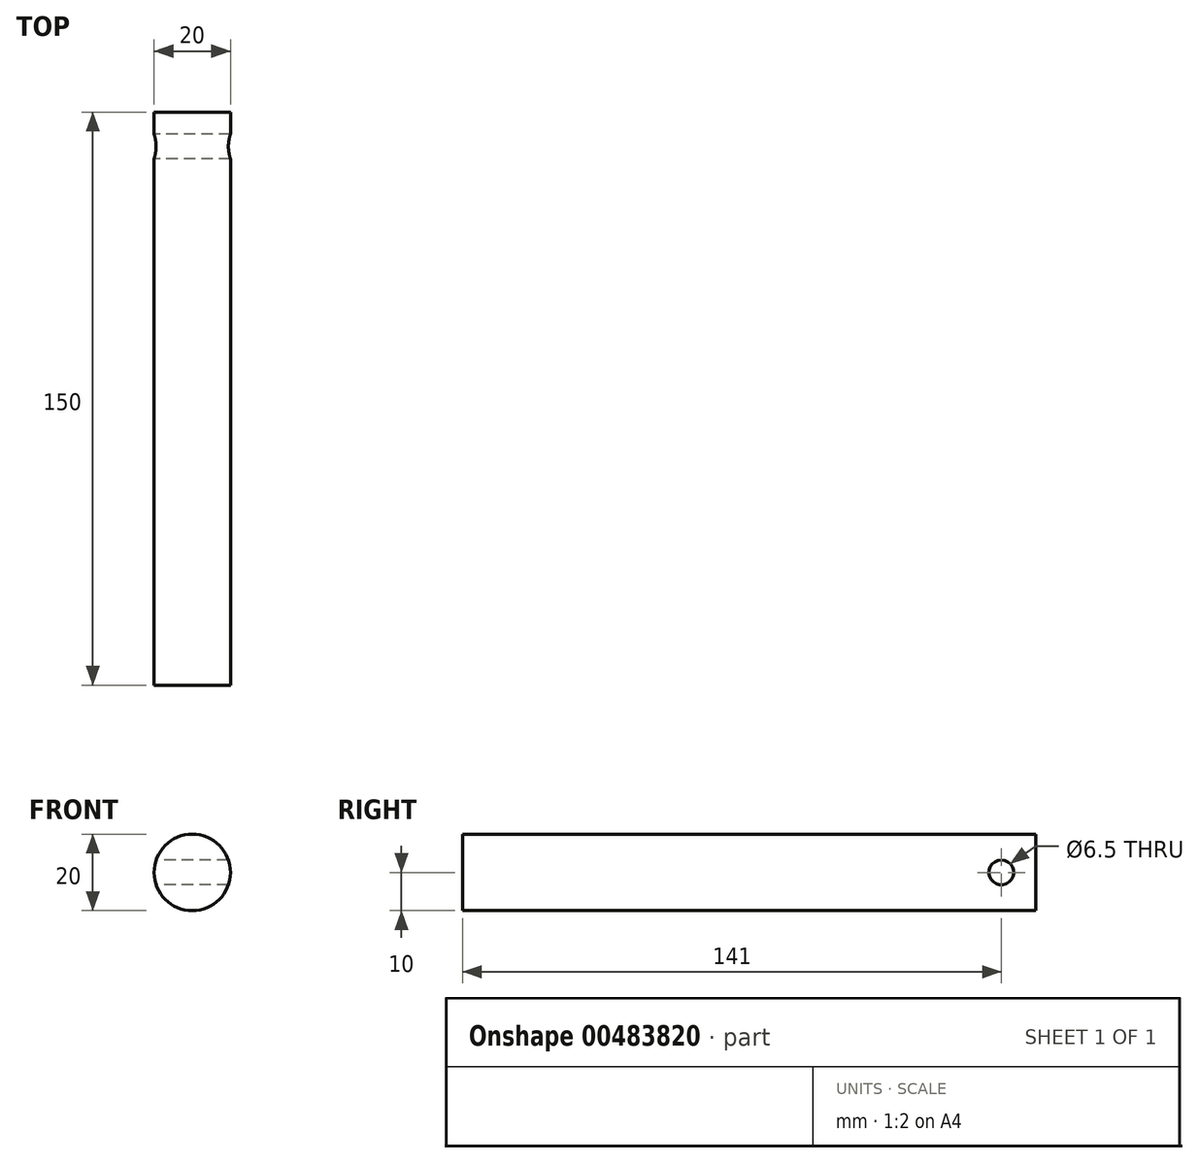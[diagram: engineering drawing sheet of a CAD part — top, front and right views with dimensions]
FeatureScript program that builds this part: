
annotation { "Feature Type Name" : "Feature", "Feature Type Description" : "" }
export const myFeature = defineFeature(function(context is Context, id is Id, definition is map)
    precondition{}
    {
        {
            var Q0;
            Q0=qCreatedBy(makeId("Front.planeOp"),FACE);
            var sketch = newSketch(context, id + "F0", { "sketchPlane" : qUnion([Q0])});
            skCircle(sketch, "E0", {"center": v(0, 0) * mm, "radius": 10 * mm});
            skSolve(sketch);
        }
        {
            var Q0;
            Q0 = qSketchRegion(id + "F0", true);
            var Q1;
            Q1 = qSketchRegion(id + "F3", true);
            var Q2;
            Q2 = qSketchRegion(id + "F2", true);
            var Q3;
            Q3 = qSketchRegion(id + "FLPr9VWBV9pL1j5_1", true);
            extrude(context, id + "F1", {"entities" : qUnion([Q0, Q1, Q2, Q3]), "depth" : 150 * mm});
        }
        {
            var Q0;
            Q0=qCreatedBy(makeId("Right.planeOp"),FACE);
            var sketch = newSketch(context, id + "F2", { "sketchPlane" : qUnion([Q0])});
            skLineSegment(sketch, "E1", {"start": v(0, 0) * mm, "end": v(-9, 0) * mm});
            skCircle(sketch, "E2", {"center": v(-9, 0) * mm, "radius": 3.25 * mm});
            skSolve(sketch);
        }
        {
            var Q0;
            Q0=qCreatedBy(makeId("Top.planeOp"),FACE);
            var sketch = newSketch(context, id + "F3", { "sketchPlane" : qUnion([Q0])});
            skLineSegment(sketch, "E3", {"start": v(0, -9.02) * mm, "end": v(10, -9.02) * mm});
            skLineSegment(sketch, "E4", {"start": v(0, -9.02) * mm, "end": v(-10, -9.02) * mm});
            skSolve(sketch);
        }
        {
            var Q0;
            Q0=sQuery(id+"F2.wireOp",VERTEX,"E2.center");
            var Q1;
            Q1=makeQuery(id+"F1.opExtrude","SWEPT_BODY",BODY,{"disambiguationData":[OSD([sQuery(id+"F0.wireOp",EDGE,"E0")])]});
            hole(context, id + "F4", {"style" : HoleStyle.SIMPLE, "endStyle" : HoleEndStyle.THROUGH, "oppositeDirection" : true, "holeDiameter" : 6.5 * mm, "isTappedThrough" : true, "tappedDepth" : 12.7 * mm, "tapClearance" : 3, "locations" : qUnion([Q0]), "scope" : qUnion([Q1])});
        }
        {
            var Q0;
            Q0=sQuery(id+"F2.wireOp",VERTEX,"E2.center");
            var Q1;
            Q1=makeQuery(id+"F1.opExtrude","SWEPT_BODY",BODY,{"disambiguationData":[OSD([sQuery(id+"F0.wireOp",EDGE,"E0")])]});
            hole(context, id + "F5", {"style" : HoleStyle.SIMPLE, "endStyle" : HoleEndStyle.THROUGH, "holeDiameter" : 6.5 * mm, "isTappedThrough" : true, "tappedDepth" : 12.7 * mm, "tapClearance" : 3, "locations" : qUnion([Q0]), "scope" : qUnion([Q1])});
        }
    });
